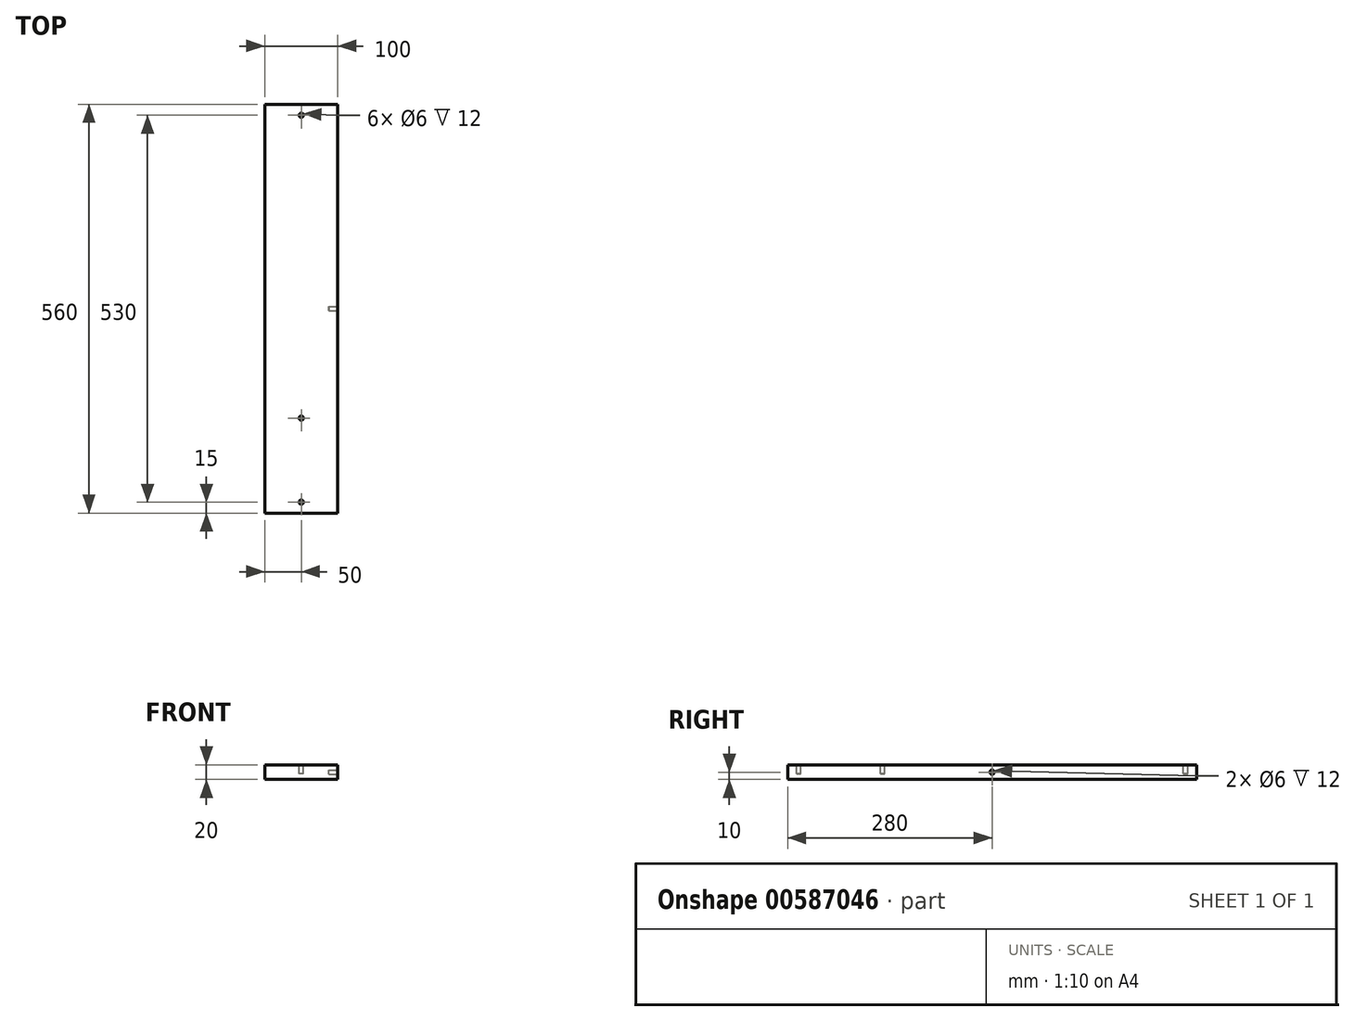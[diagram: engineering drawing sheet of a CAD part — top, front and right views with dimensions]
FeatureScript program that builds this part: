
annotation { "Feature Type Name" : "Feature", "Feature Type Description" : "" }
export const myFeature = defineFeature(function(context is Context, id is Id, definition is map)
    precondition{}
    {
        {
            var Q0;
            Q0=qCreatedBy(makeId("Top.planeOp"),FACE);
            var sketch = newSketch(context, id + "F0", { "sketchPlane" : qUnion([Q0])});
            skLineSegment(sketch, "E0.bottom", {"start": v(0, 0) * mm, "end": v(100, 0) * mm});
            skLineSegment(sketch, "E0.top", {"start": v(0, 560) * mm, "end": v(100, 560) * mm});
            skLineSegment(sketch, "E0.left", {"start": v(0, 0) * mm, "end": v(0, 560) * mm});
            skLineSegment(sketch, "E0.right", {"start": v(100, 0) * mm, "end": v(100, 560) * mm});
            skSolve(sketch);
        }
        {
            var Q0;
            Q0=makeQuery(id+"F0.imprint","IMPRINT",FACE,{"disambiguationData":[TD([[makeQuery(id+"F0.imprint","IMPRINT",EDGE,{"derivedFrom":sQuery(id+"F0.wireOp",EDGE,"E0.bottom")}),1.0]])]});
            extrude(context, id + "F1", {"entities" : qUnion([Q0]), "depth" : 20 * mm, "offsetDistance" : 25 * mm});
        }
        {
            var Q0;
            Q0=makeQuery(id+"F1.opExtrude","CAP_FACE",FACE,{"disambiguationData":[OSD([sQuery(id+"F0.wireOp",EDGE,"E0.bottom"),sQuery(id+"F0.wireOp",EDGE,"E0.top"),sQuery(id+"F0.wireOp",EDGE,"E0.left"),sQuery(id+"F0.wireOp",EDGE,"E0.right")])],"isStart":false});
            var sketch = newSketch(context, id + "F2", { "sketchPlane" : qUnion([Q0])});
            skCircle(sketch, "E1", {"center": v(50, 15) * mm, "radius": 3 * mm});
            skPoint(sketch, "E1.centerSnap0", {"position": v(50, 0) * mm});
            skSolve(sketch);
        }
        {
            var Q0;
            Q0=makeQuery(id+"F2.imprint","IMPRINT",FACE,{"disambiguationData":[TD([[makeQuery(id+"F2.imprint","IMPRINT",EDGE,{"derivedFrom":sQuery(id+"F2.wireOp",EDGE,"E1")}),1.0]])]});
            extrude(context, id + "F3", {"entities" : qUnion([Q0]), "operationType" : NewBodyOperationType.REMOVE, "oppositeDirection" : true, "depth" : 12 * mm, "offsetDistance" : 25 * mm});
        }
        {
            var Q0;
            Q0=makeQuery(id+"F1.opExtrude","CAP_FACE",FACE,{"disambiguationData":[OSD([sQuery(id+"F0.wireOp",EDGE,"E0.bottom"),sQuery(id+"F0.wireOp",EDGE,"E0.top"),sQuery(id+"F0.wireOp",EDGE,"E0.left"),sQuery(id+"F0.wireOp",EDGE,"E0.right")])],"isStart":false});
            var sketch = newSketch(context, id + "F4", { "sketchPlane" : qUnion([Q0])});
            skCircle(sketch, "E2", {"center": v(50, 545) * mm, "radius": 3 * mm});
            skPoint(sketch, "E2.centerSnap0", {"position": v(50, 560) * mm});
            skSolve(sketch);
        }
        {
            var Q0;
            Q0=makeQuery(id+"F4.imprint","IMPRINT",FACE,{"disambiguationData":[TD([[makeQuery(id+"F4.imprint","IMPRINT",EDGE,{"derivedFrom":sQuery(id+"F4.wireOp",EDGE,"E2")}),1.0]])]});
            extrude(context, id + "F5", {"entities" : qUnion([Q0]), "operationType" : NewBodyOperationType.REMOVE, "oppositeDirection" : true, "depth" : 12 * mm, "offsetDistance" : 25 * mm});
        }
        {
            var Q0;
            Q0=makeQuery(id+"F1.opExtrude","CAP_FACE",FACE,{"disambiguationData":[OSD([sQuery(id+"F0.wireOp",EDGE,"E0.bottom"),sQuery(id+"F0.wireOp",EDGE,"E0.top"),sQuery(id+"F0.wireOp",EDGE,"E0.left"),sQuery(id+"F0.wireOp",EDGE,"E0.right")])],"isStart":false});
            var sketch = newSketch(context, id + "F6", { "sketchPlane" : qUnion([Q0])});
            skCircle(sketch, "E3", {"center": v(50, 130) * mm, "radius": 3 * mm});
            skPoint(sketch, "E3.centerSnap0", {"position": v(50, 0) * mm});
            skSolve(sketch);
        }
        {
            var Q0;
            Q0=makeQuery(id+"F6.imprint","IMPRINT",FACE,{"disambiguationData":[TD([[makeQuery(id+"F6.imprint","IMPRINT",EDGE,{"derivedFrom":sQuery(id+"F6.wireOp",EDGE,"E3")}),1.0]])]});
            extrude(context, id + "F7", {"entities" : qUnion([Q0]), "operationType" : NewBodyOperationType.REMOVE, "oppositeDirection" : true, "depth" : 12 * mm, "offsetDistance" : 25 * mm});
        }
        {
            var Q0;
            Q0=makeQuery(id+"F1.opExtrude","SWEPT_FACE",FACE,{"disambiguationData":[OSD([sQuery(id+"F0.wireOp",EDGE,"E0.right")])]});
            var sketch = newSketch(context, id + "F8", { "sketchPlane" : qUnion([Q0])});
            skCircle(sketch, "E4", {"center": v(280, 10) * mm, "radius": 3 * mm});
            skPoint(sketch, "E4.centerSnap0", {"position": v(280, 20) * mm});
            skPoint(sketch, "E4.centerSnap1", {"position": v(0, 10) * mm});
            skSolve(sketch);
        }
        {
            var Q0;
            Q0=makeQuery(id+"F8.imprint","IMPRINT",FACE,{"disambiguationData":[TD([[makeQuery(id+"F8.imprint","IMPRINT",EDGE,{"derivedFrom":sQuery(id+"F8.wireOp",EDGE,"E4")}),1.0]])]});
            extrude(context, id + "F9", {"entities" : qUnion([Q0]), "operationType" : NewBodyOperationType.REMOVE, "oppositeDirection" : true, "depth" : 12 * mm, "offsetDistance" : 25 * mm});
        }
    });
